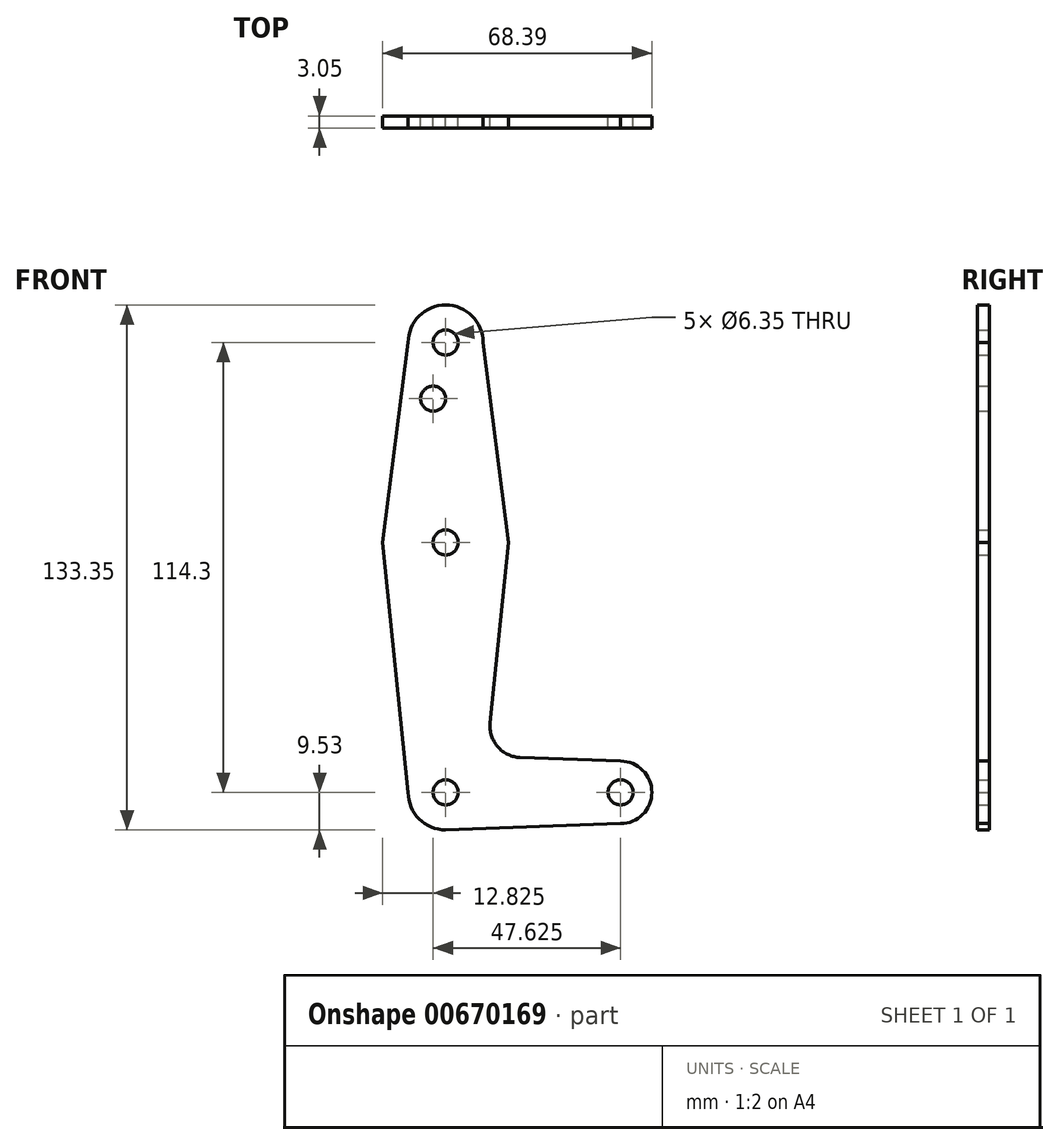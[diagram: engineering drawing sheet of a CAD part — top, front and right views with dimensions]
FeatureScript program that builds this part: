
annotation { "Feature Type Name" : "Feature", "Feature Type Description" : "" }
export const myFeature = defineFeature(function(context is Context, id is Id, definition is map)
    precondition{}
    {
        {
            var Q0;
            Q0=qCreatedBy(makeId("Front.planeOp"),FACE);
            var sketch = newSketch(context, id + "F0", { "sketchPlane" : qUnion([Q0])});
            skCircle(sketch, "E0", {"center": v(0, 0) * mm, "radius": 15.88 * mm});
            skCircle(sketch, "E1", {"center": v(0, -63.5) * mm, "radius": 9.53 * mm});
            skCircle(sketch, "E2", {"center": v(0, 50.8) * mm, "radius": 9.53 * mm});
            skCircle(sketch, "E3", {"center": v(44.45, -63.5) * mm, "radius": 7.94 * mm});
            skCircle(sketch, "E4", {"center": v(0, 50.8) * mm, "radius": 3.17 * mm});
            skCircle(sketch, "E5", {"center": v(0, 0) * mm, "radius": 3.17 * mm});
            skCircle(sketch, "E6", {"center": v(0, -63.5) * mm, "radius": 3.17 * mm});
            skCircle(sketch, "E7", {"center": v(44.45, -63.5) * mm, "radius": 3.17 * mm});
            skCircle(sketch, "E8", {"center": v(-3.17, 36.53) * mm, "radius": 3.17 * mm});
            skLineSegment(sketch, "E9", {"start": v(-9.53, 50.8) * mm, "end": v(-16, 0) * mm});
            skLineSegment(sketch, "E10", {"start": v(9.53, 50.8) * mm, "end": v(16, 0) * mm});
            skLineSegment(sketch, "E11", {"start": v(-16, 0) * mm, "end": v(-9.52, -63.5) * mm});
            skLineSegment(sketch, "E12", {"start": v(0, -73.03) * mm, "end": v(44.45, -71.44) * mm});
            skLineSegment(sketch, "E13", {"start": v(16, 0) * mm, "end": v(11.32, -45.9) * mm});
            skLineSegment(sketch, "E14", {"start": v(44.45, -55.56) * mm, "end": v(18.95, -54.65) * mm});
            skPoint(sketch, "E15.newPointA", {"position": v(9.52, -63.5) * mm});
            skPoint(sketch, "E15.newPointB", {"position": v(0, -53.98) * mm});
            skArc(sketch, "E15.filletArc", {"start": v(11.32, -45.9) * mm, "mid": v(13.24, -51.93) * mm, "end": v(18.95, -54.65) * mm});
            skSolve(sketch);
        }
        {
            var Q0;
            Q0=makeQuery(id+"F0.imprint","IMPRINT",FACE,{"disambiguationData":[TD([[makeQuery(id+"F0.imprint","IMPRINT",EDGE,{"derivedFrom":sQuery(id+"F0.wireOp",EDGE,"E4")}),-1.0]])]});
            var Q1;
            Q1=makeQuery(id+"F0.imprint","IMPRINT",FACE,{"disambiguationData":[TD([[makeQuery(id+"F0.imprint","IMPRINT",EDGE,{"derivedFrom":sQuery(id+"F0.wireOp",EDGE,"E8")}),-1.0]])]});
            var Q2;
            Q2=makeQuery(id+"F0.imprint","IMPRINT",FACE,{"disambiguationData":[TD([[makeQuery(id+"F0.imprint","IMPRINT",EDGE,{"derivedFrom":sQuery(id+"F0.wireOp",EDGE,"E5")}),-1.0]])]});
            var Q3;
            {var subQ0=sQuery(id+"F0.wireOp",EDGE,"E11");Q3=makeQuery(id+"F0.imprint","IMPRINT",FACE,{"disambiguationData":[TD([[makeQuery(id+"F0.imprint","IMPRINT",EDGE,{"derivedFrom":subQ0}),1.0]])]});}
            var Q4;
            Q4=makeQuery(id+"F0.imprint","IMPRINT",FACE,{"disambiguationData":[TD([[makeQuery(id+"F0.imprint","IMPRINT",EDGE,{"derivedFrom":sQuery(id+"F0.wireOp",EDGE,"E6")}),-1.0]])]});
            var Q5;
            Q5=makeQuery(id+"F0.imprint","IMPRINT",FACE,{"disambiguationData":[TD([[makeQuery(id+"F0.imprint","IMPRINT",EDGE,{"derivedFrom":sQuery(id+"F0.wireOp",EDGE,"E7")}),-1.0]])]});
            extrude(context, id + "F1", {"entities" : qUnion([Q0, Q1, Q2, Q3, Q4, Q5]), "depth" : 3.05 * mm, "offsetDistance" : 25 * mm});
        }
    });
